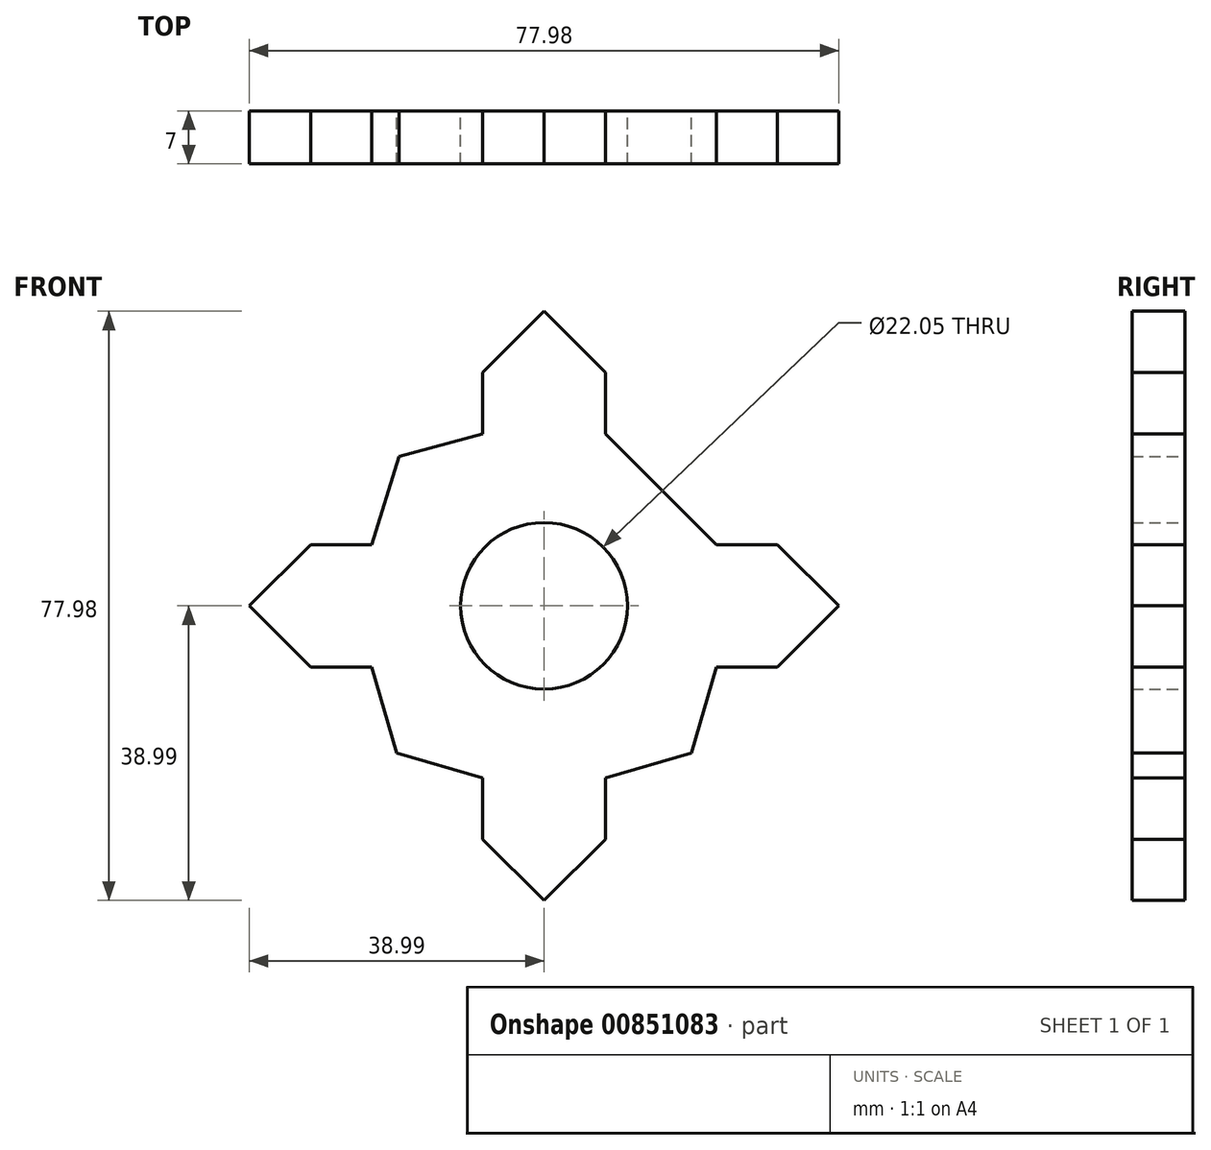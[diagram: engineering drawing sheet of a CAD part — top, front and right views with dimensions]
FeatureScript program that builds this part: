
annotation { "Feature Type Name" : "Feature", "Feature Type Description" : "" }
export const myFeature = defineFeature(function(context is Context, id is Id, definition is map)
    precondition{}
    {
        {
            var Q0;
            Q0=qCreatedBy(makeId("Front.planeOp"),FACE);
            var sketch = newSketch(context, id + "F0", { "sketchPlane" : qUnion([Q0])});
            skCircle(sketch, "E0", {"center": v(0, 0) * mm, "radius": 13.74 * mm});
            skLineSegment(sketch, "E1", {"start": v(0, 30.88) * mm, "end": v(-30.88, 0) * mm});
            skLineSegment(sketch, "E2", {"start": v(-30.88, 0) * mm, "end": v(0, -30.88) * mm});
            skLineSegment(sketch, "E3", {"start": v(30.88, 0) * mm, "end": v(0, -30.88) * mm});
            skLineSegment(sketch, "E4", {"start": v(30.88, 0) * mm, "end": v(0, 30.88) * mm});
            skLineSegment(sketch, "E5", {"start": v(-8.1, 30.88) * mm, "end": v(0, 38.99) * mm});
            skLineSegment(sketch, "E6", {"start": v(0, 38.99) * mm, "end": v(8.1, 30.88) * mm});
            skLineSegment(sketch, "E7", {"start": v(30.88, 8.1) * mm, "end": v(38.99, 0) * mm});
            skLineSegment(sketch, "E8", {"start": v(38.99, 0) * mm, "end": v(30.88, -8.1) * mm});
            skLineSegment(sketch, "E9", {"start": v(-30.88, 8.1) * mm, "end": v(-38.99, 0) * mm});
            skLineSegment(sketch, "E10", {"start": v(-38.99, 0) * mm, "end": v(-30.88, -8.1) * mm});
            skLineSegment(sketch, "E11", {"start": v(-8.1, -30.88) * mm, "end": v(0, -38.99) * mm});
            skLineSegment(sketch, "E12", {"start": v(0, -38.99) * mm, "end": v(8.1, -30.88) * mm});
            skCircle(sketch, "E13", {"center": v(0, 0) * mm, "radius": 11.03 * mm});
            skLineSegment(sketch, "E14", {"start": v(-8.1, 30.88) * mm, "end": v(-8.1, 22.78) * mm});
            skLineSegment(sketch, "E15", {"start": v(8.1, 30.88) * mm, "end": v(8.1, 22.78) * mm});
            skLineSegment(sketch, "E16", {"start": v(30.88, 8.1) * mm, "end": v(22.78, 8.1) * mm});
            skLineSegment(sketch, "E17", {"start": v(30.88, -8.1) * mm, "end": v(22.78, -8.1) * mm});
            skLineSegment(sketch, "E18", {"start": v(-8.1, -30.88) * mm, "end": v(-8.1, -22.78) * mm});
            skLineSegment(sketch, "E19", {"start": v(8.1, -30.88) * mm, "end": v(8.1, -22.78) * mm});
            skLineSegment(sketch, "E20", {"start": v(-30.88, 8.1) * mm, "end": v(-22.78, 8.1) * mm});
            skLineSegment(sketch, "E21", {"start": v(-30.88, -8.1) * mm, "end": v(-22.78, -8.1) * mm});
            skLineSegment(sketch, "E22", {"start": v(0, 0) * mm, "end": v(0, -38.99) * mm});
            skLineSegment(sketch, "E23", {"start": v(-22.78, -8.1) * mm, "end": v(-19.5, -19.5) * mm});
            skLineSegment(sketch, "E24", {"start": v(-19.5, -19.5) * mm, "end": v(-8.1, -22.78) * mm});
            skLineSegment(sketch, "E25", {"start": v(15.44, 15.44) * mm, "end": v(8.1, 22.78) * mm});
            skLineSegment(sketch, "E26", {"start": v(8.1, 22.78) * mm, "end": v(19.5, 19.5) * mm});
            skLineSegment(sketch, "E27", {"start": v(19.5, 19.5) * mm, "end": v(22.78, 8.1) * mm});
            skLineSegment(sketch, "E28", {"start": v(-22.78, 8.1) * mm, "end": v(-19.2, 19.79) * mm});
            skLineSegment(sketch, "E29", {"start": v(-19.2, 19.79) * mm, "end": v(-8.1, 22.78) * mm});
            skLineSegment(sketch, "E30", {"start": v(8.1, -22.78) * mm, "end": v(19.5, -19.5) * mm});
            skLineSegment(sketch, "E31", {"start": v(19.5, -19.5) * mm, "end": v(22.78, -8.1) * mm});
            skSolve(sketch);
        }
        {
            var Q0;
            {var subQ2=sQuery(id+"F0.wireOp",EDGE,"E28");Q0=makeQuery(id+"F0.imprint","IMPRINT",FACE,{"disambiguationData":[TD([[makeQuery(id+"F0.imprint","IMPRINT",EDGE,{"derivedFrom":subQ2}),-1.0]])]});}
            var Q1;
            Q1=makeQuery(id+"F0.imprint","IMPRINT",FACE,{"disambiguationData":[TD([[makeQuery(id+"F0.imprint","IMPRINT",EDGE,{"derivedFrom":sQuery(id+"F0.wireOp",EDGE,"E5")}),-1.0]])]});
            var Q2;
            {var subQ2=sQuery(id+"F0.wireOp",EDGE,"E25");Q2=makeQuery(id+"F0.imprint","IMPRINT",FACE,{"disambiguationData":[TD([[makeQuery(id+"F0.imprint","IMPRINT",EDGE,{"derivedFrom":subQ2}),-1.0]])]});}
            var Q3;
            Q3=makeQuery(id+"F0.imprint","IMPRINT",FACE,{"disambiguationData":[TD([[makeQuery(id+"F0.imprint","IMPRINT",EDGE,{"derivedFrom":sQuery(id+"F0.wireOp",EDGE,"E7")}),-1.0]])]});
            var Q4;
            {var subQ2=sQuery(id+"F0.wireOp",EDGE,"E30");Q4=makeQuery(id+"F0.imprint","IMPRINT",FACE,{"disambiguationData":[TD([[makeQuery(id+"F0.imprint","IMPRINT",EDGE,{"derivedFrom":subQ2}),1.0]])]});}
            var Q5;
            {var subQ4=sQuery(id+"F0.wireOp",EDGE,"E12");Q5=makeQuery(id+"F0.imprint","IMPRINT",FACE,{"disambiguationData":[TD([[makeQuery(id+"F0.imprint","IMPRINT",EDGE,{"derivedFrom":subQ4}),1.0]])]});}
            var Q6;
            {var subQ2=sQuery(id+"F0.wireOp",EDGE,"E23");Q6=makeQuery(id+"F0.imprint","IMPRINT",FACE,{"disambiguationData":[TD([[makeQuery(id+"F0.imprint","IMPRINT",EDGE,{"derivedFrom":subQ2}),1.0]])]});}
            var Q7;
            Q7=makeQuery(id+"F0.imprint","IMPRINT",FACE,{"disambiguationData":[TD([[makeQuery(id+"F0.imprint","IMPRINT",EDGE,{"derivedFrom":sQuery(id+"F0.wireOp",EDGE,"E9")}),1.0]])]});
            var Q8;
            Q8=makeQuery(id+"F0.imprint","IMPRINT",FACE,{"disambiguationData":[TD([[makeQuery(id+"F0.imprint","IMPRINT",EDGE,{"derivedFrom":sQuery(id+"F0.wireOp",EDGE,"E0")}),-1.0]])]});
            var Q9;
            {var subQ4=sQuery(id+"F0.wireOp",EDGE,"E11");Q9=makeQuery(id+"F0.imprint","IMPRINT",FACE,{"disambiguationData":[TD([[makeQuery(id+"F0.imprint","IMPRINT",EDGE,{"derivedFrom":subQ4}),1.0]])]});}
            var Q10;
            Q10=makeQuery(id+"F0.imprint","IMPRINT",FACE,{"disambiguationData":[TD([[makeQuery(id+"F0.imprint","IMPRINT",EDGE,{"derivedFrom":sQuery(id+"F0.wireOp",EDGE,"E0")}),1.0]])]});
            extrude(context, id + "F1", {"entities" : qUnion([Q0, Q1, Q2, Q3, Q4, Q5, Q6, Q7, Q8, Q9, Q10]), "depth" : 7 * mm, "offsetDistance" : 25 * mm});
        }
    });
